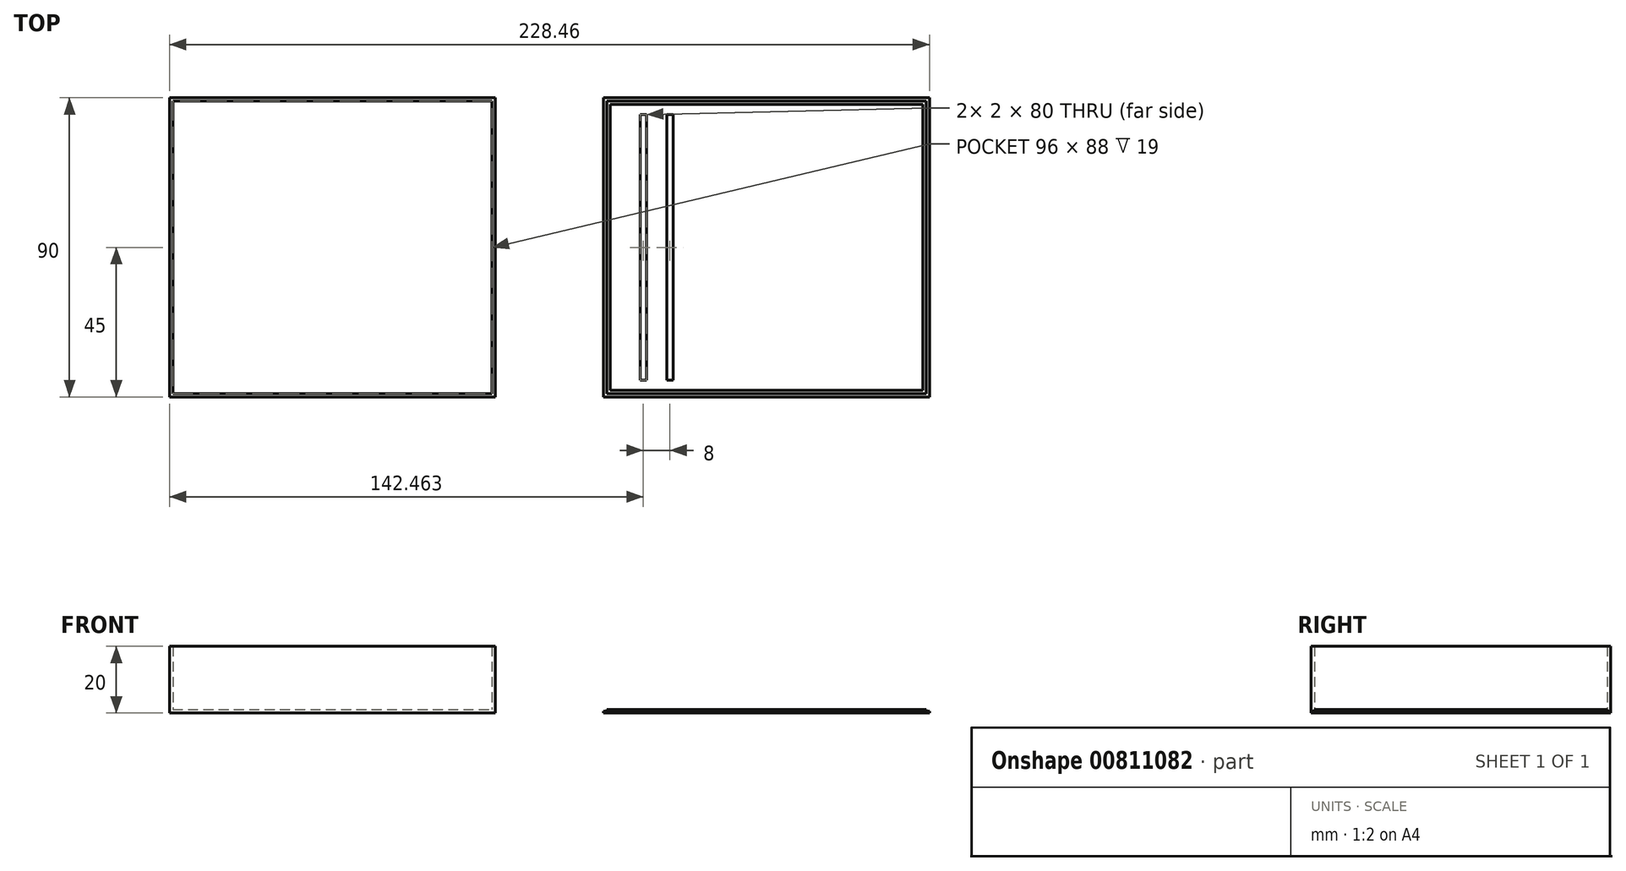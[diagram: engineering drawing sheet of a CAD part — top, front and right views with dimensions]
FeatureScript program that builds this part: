
annotation { "Feature Type Name" : "Feature", "Feature Type Description" : "" }
export const myFeature = defineFeature(function(context is Context, id is Id, definition is map)
    precondition{}
    {
        {
            var Q0;
            Q0=qCreatedBy(makeId("Top.planeOp"),FACE);
            var sketch = newSketch(context, id + "F0", { "sketchPlane" : qUnion([Q0])});
            skLineSegment(sketch, "E0.bottom", {"start": v(59.81, 58.4) * mm, "end": v(157.81, 58.4) * mm});
            skLineSegment(sketch, "E0.top", {"start": v(59.81, -31.6) * mm, "end": v(157.81, -31.6) * mm});
            skLineSegment(sketch, "E0.left", {"start": v(59.81, 58.4) * mm, "end": v(59.81, -31.6) * mm});
            skLineSegment(sketch, "E0.right", {"start": v(157.81, 58.4) * mm, "end": v(157.81, -31.6) * mm});
            skLineSegment(sketch, "E1.0", {"start": v(60.81, 57.4) * mm, "end": v(156.81, 57.4) * mm});
            skLineSegment(sketch, "E1.1", {"start": v(60.81, 57.4) * mm, "end": v(60.81, -30.6) * mm});
            skLineSegment(sketch, "E1.2", {"start": v(60.81, -30.6) * mm, "end": v(156.81, -30.6) * mm});
            skLineSegment(sketch, "E1.3", {"start": v(156.81, 57.4) * mm, "end": v(156.81, -30.6) * mm});
            skLineSegment(sketch, "E2.bottom", {"start": v(-70.65, 58.4) * mm, "end": v(27.35, 58.4) * mm});
            skLineSegment(sketch, "E2.top", {"start": v(-70.65, -31.6) * mm, "end": v(27.35, -31.6) * mm});
            skLineSegment(sketch, "E2.left", {"start": v(-70.65, 58.4) * mm, "end": v(-70.65, -31.6) * mm});
            skLineSegment(sketch, "E2.right", {"start": v(27.35, 58.4) * mm, "end": v(27.35, -31.6) * mm});
            skLineSegment(sketch, "E3.0", {"start": v(-69.65, 57.4) * mm, "end": v(26.35, 57.4) * mm});
            skLineSegment(sketch, "E3.1", {"start": v(-69.65, 57.4) * mm, "end": v(-69.65, -30.6) * mm});
            skLineSegment(sketch, "E3.2", {"start": v(-69.65, -30.6) * mm, "end": v(26.35, -30.6) * mm});
            skLineSegment(sketch, "E3.3", {"start": v(26.35, 57.4) * mm, "end": v(26.35, -30.6) * mm});
            skLineSegment(sketch, "E4", {"start": v(78.81, -26.6) * mm, "end": v(80.81, -26.6) * mm});
            skLineSegment(sketch, "E5", {"start": v(80.81, -26.6) * mm, "end": v(80.81, 53.4) * mm});
            skLineSegment(sketch, "E6", {"start": v(78.81, -26.6) * mm, "end": v(78.81, 53.4) * mm});
            skLineSegment(sketch, "E7", {"start": v(78.81, 53.4) * mm, "end": v(80.81, 53.4) * mm});
            skLineSegment(sketch, "E8", {"start": v(70.81, -26.6) * mm, "end": v(72.81, -26.6) * mm});
            skLineSegment(sketch, "E9", {"start": v(72.81, -26.6) * mm, "end": v(72.81, 53.4) * mm});
            skLineSegment(sketch, "E10", {"start": v(70.81, -26.6) * mm, "end": v(70.81, 53.4) * mm});
            skLineSegment(sketch, "E11", {"start": v(70.81, 53.4) * mm, "end": v(72.81, 53.4) * mm});
            skSolve(sketch);
        }
        {
            var Q0;
            Q0=makeQuery(id+"F0.imprint","IMPRINT",FACE,{"disambiguationData":[TD([[makeQuery(id+"F0.imprint","IMPRINT",EDGE,{"derivedFrom":sQuery(id+"F0.wireOp",EDGE,"E2.bottom")}),-1.0]])]});
            extrude(context, id + "F1", {"entities" : qUnion([Q0]), "depth" : 20 * mm, "offsetDistance" : 25 * mm});
        }
        {
            var Q0;
            Q0=makeQuery(id+"F0.imprint","IMPRINT",FACE,{"disambiguationData":[TD([[makeQuery(id+"F0.imprint","IMPRINT",EDGE,{"derivedFrom":sQuery(id+"F0.wireOp",EDGE,"E3.0")}),-1.0]])]});
            extrude(context, id + "F2", {"entities" : qUnion([Q0]), "operationType" : NewBodyOperationType.ADD, "depth" : 1 * mm, "offsetDistance" : 25 * mm});
        }
        {
            var Q0;
            Q0=makeQuery(id+"F0.imprint","IMPRINT",FACE,{"disambiguationData":[TD([[makeQuery(id+"F0.imprint","IMPRINT",EDGE,{"derivedFrom":sQuery(id+"F0.wireOp",EDGE,"E0.bottom")}),-1.0]])]});
            extrude(context, id + "F3", {"entities" : qUnion([Q0]), "depth" : 0.5 * mm, "offsetDistance" : 25 * mm});
        }
        {
            var Q0;
            Q0=makeQuery(id+"F0.imprint","IMPRINT",FACE,{"disambiguationData":[TD([[makeQuery(id+"F0.imprint","IMPRINT",EDGE,{"derivedFrom":sQuery(id+"F0.wireOp",EDGE,"E1.0")}),-1.0]])]});
            extrude(context, id + "F4", {"entities" : qUnion([Q0]), "operationType" : NewBodyOperationType.ADD, "depth" : 1 * mm, "offsetDistance" : 25 * mm});
        }
        {
            var Q0;
            Q0=makeQuery(id+"F4.opExtrude","CAP_FACE",FACE,{"disambiguationData":[OSD([sQuery(id+"F0.wireOp",EDGE,"E1.0"),sQuery(id+"F0.wireOp",EDGE,"E1.1"),sQuery(id+"F0.wireOp",EDGE,"E1.2"),sQuery(id+"F0.wireOp",EDGE,"E1.3"),sQuery(id+"F0.wireOp",EDGE,"E4"),sQuery(id+"F0.wireOp",EDGE,"E5"),sQuery(id+"F0.wireOp",EDGE,"E6"),sQuery(id+"F0.wireOp",EDGE,"E7"),sQuery(id+"F0.wireOp",EDGE,"E8"),sQuery(id+"F0.wireOp",EDGE,"E9"),sQuery(id+"F0.wireOp",EDGE,"E10"),sQuery(id+"F0.wireOp",EDGE,"E11")])],"isStart":false});
            var sketch = newSketch(context, id + "F5", { "sketchPlane" : qUnion([Q0])});
            skLineSegment(sketch, "E12.0", {"start": v(155.81, -29.6) * mm, "end": v(155.81, 56.4) * mm});
            skLineSegment(sketch, "E12.1", {"start": v(61.81, -29.6) * mm, "end": v(155.81, -29.6) * mm});
            skLineSegment(sketch, "E12.2", {"start": v(61.81, 56.4) * mm, "end": v(61.81, -29.6) * mm});
            skLineSegment(sketch, "E12.3", {"start": v(155.81, 56.4) * mm, "end": v(61.81, 56.4) * mm});
            skSolve(sketch);
        }
        {
            var Q0;
            Q0=makeQuery(id+"F5.imprint","IMPRINT",FACE,{"disambiguationData":[TD([[makeQuery(id+"F5.imprint","IMPRINT",EDGE,{"derivedFrom":sQuery(id+"F5.wireOp",EDGE,"E12.0")}),1.0]])]});
            extrude(context, id + "F6", {"entities" : qUnion([Q0]), "operationType" : NewBodyOperationType.REMOVE, "oppositeDirection" : true, "depth" : 0.5 * mm, "offsetDistance" : 25 * mm});
        }
    });
